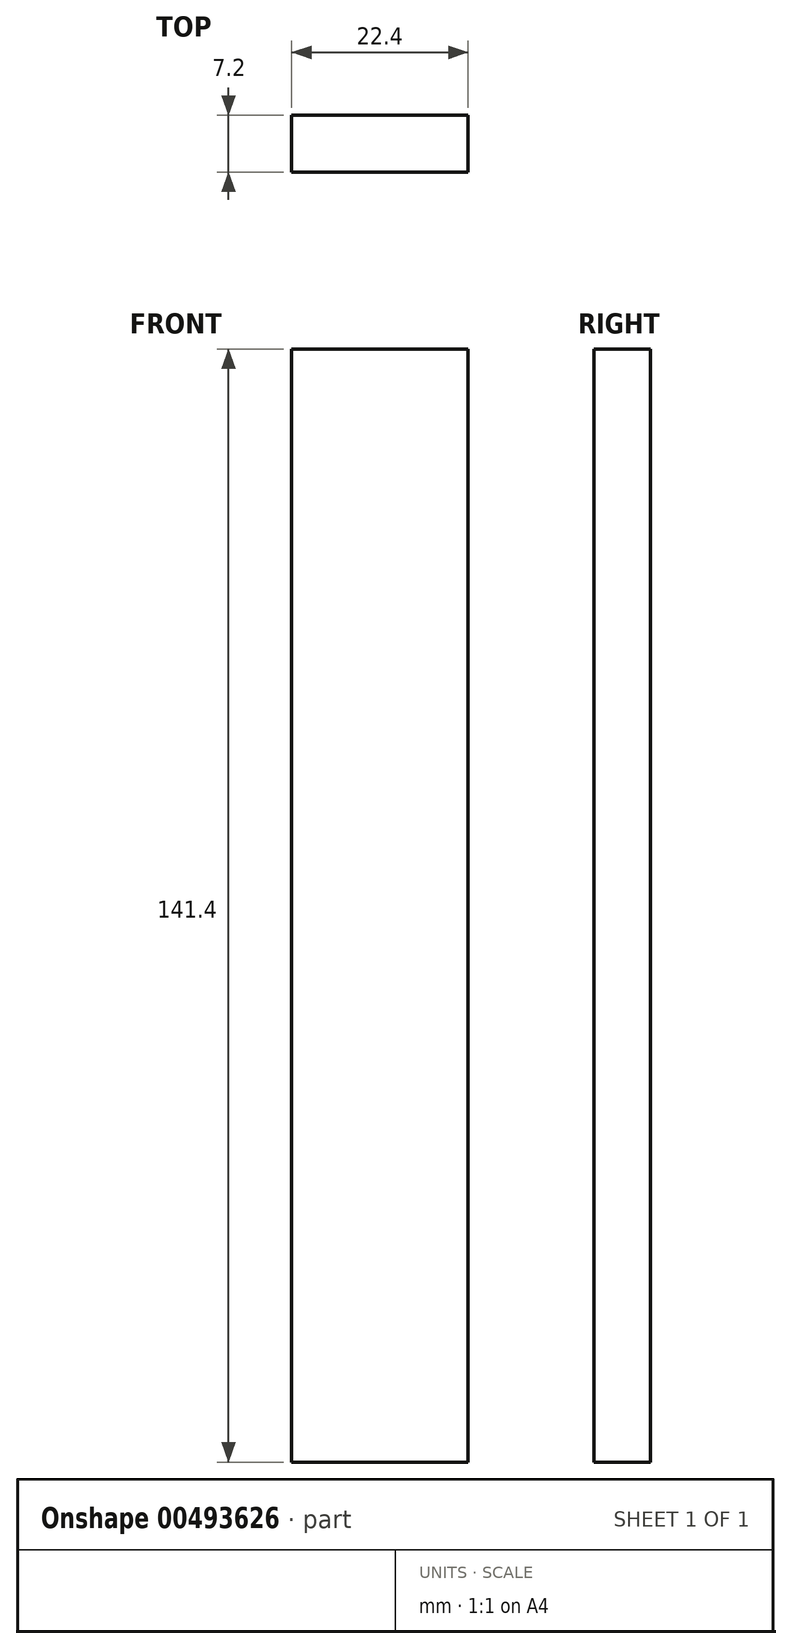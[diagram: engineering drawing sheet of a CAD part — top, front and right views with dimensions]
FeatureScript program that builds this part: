
annotation { "Feature Type Name" : "Feature", "Feature Type Description" : "" }
export const myFeature = defineFeature(function(context is Context, id is Id, definition is map)
    precondition{}
    {
        {
            var Q0;
            Q0=qCreatedBy(makeId("Front.planeOp"),FACE);
            var sketch = newSketch(context, id + "F0", { "sketchPlane" : qUnion([Q0])});
            skLineSegment(sketch, "E0.bottom", {"start": v(11.2, -58.2) * mm, "end": v(-11.2, -58.2) * mm});
            skLineSegment(sketch, "E0.top", {"start": v(11.2, 58.2) * mm, "end": v(-11.2, 58.2) * mm});
            skLineSegment(sketch, "E0.left", {"start": v(11.2, -58.2) * mm, "end": v(11.2, 58.2) * mm});
            skLineSegment(sketch, "E0.right", {"start": v(-11.2, -58.2) * mm, "end": v(-11.2, 58.2) * mm});
            skPoint(sketch, "E0.middle", {"position": v(0, 0) * mm});
            skSolve(sketch);
        }
        {
            var Q0;
            Q0=qSketchRegion(id+"F0",true);
            var Q1;
            Q1=makeQuery(id+"F0.imprint","IMPRINT",FACE,{"disambiguationData":[TD([[makeQuery(id+"F0.imprint","IMPRINT",EDGE,{"derivedFrom":sQuery(id+"F0.wireOp",EDGE,"E0.bottom")}),-1.0]])]});
            extrude(context, id + "F1", {"entities" : qUnion([Q0, Q1]), "depth" : 7.2 * mm});
        }
        {
            var Q0;
            Q0=makeQuery(id+"F1.opExtrude","SWEPT_FACE",FACE,{"disambiguationData":[OSD([sQuery(id+"F0.wireOp",EDGE,"E0.top")])]});
            extrude(context, id + "F2", {"entities" : qUnion([Q0]), "operationType" : NewBodyOperationType.ADD, "depth" : 25 * mm});
        }
    });
